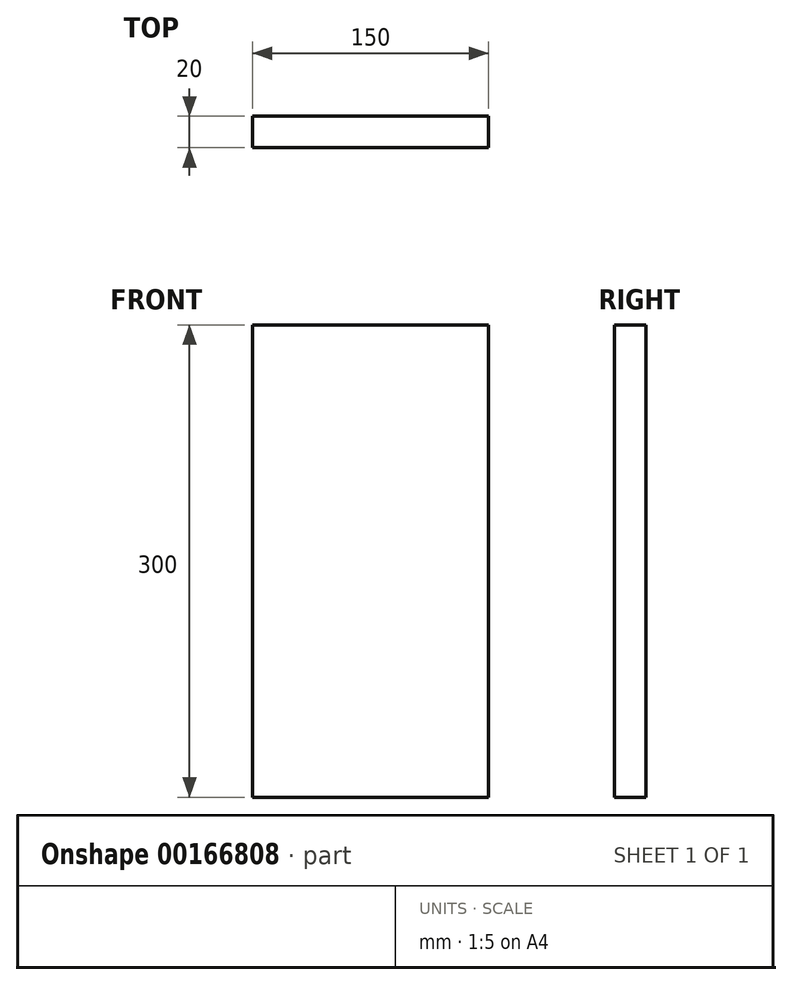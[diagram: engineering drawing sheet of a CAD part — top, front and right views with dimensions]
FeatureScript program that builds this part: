
annotation { "Feature Type Name" : "Feature", "Feature Type Description" : "" }
export const myFeature = defineFeature(function(context is Context, id is Id, definition is map)
    precondition{}
    {
        {
            var Q0;
            Q0=qCreatedBy(makeId("Front.planeOp"),FACE);
            var sketch = newSketch(context, id + "F0", { "sketchPlane" : qUnion([Q0])});
            skLineSegment(sketch, "E0.bottom", {"start": v(0, 0) * mm, "end": v(150, 0) * mm});
            skLineSegment(sketch, "E0.top", {"start": v(0, 300) * mm, "end": v(150, 300) * mm});
            skLineSegment(sketch, "E0.left", {"start": v(0, 0) * mm, "end": v(0, 300) * mm});
            skLineSegment(sketch, "E0.right", {"start": v(150, 0) * mm, "end": v(150, 300) * mm});
            skSolve(sketch);
        }
        {
            var Q0;
            Q0 = qSketchRegion(id + "F0", true);
            extrude(context, id + "F1", {"entities" : qUnion([Q0]), "depth" : 20 * mm});
        }
    });
